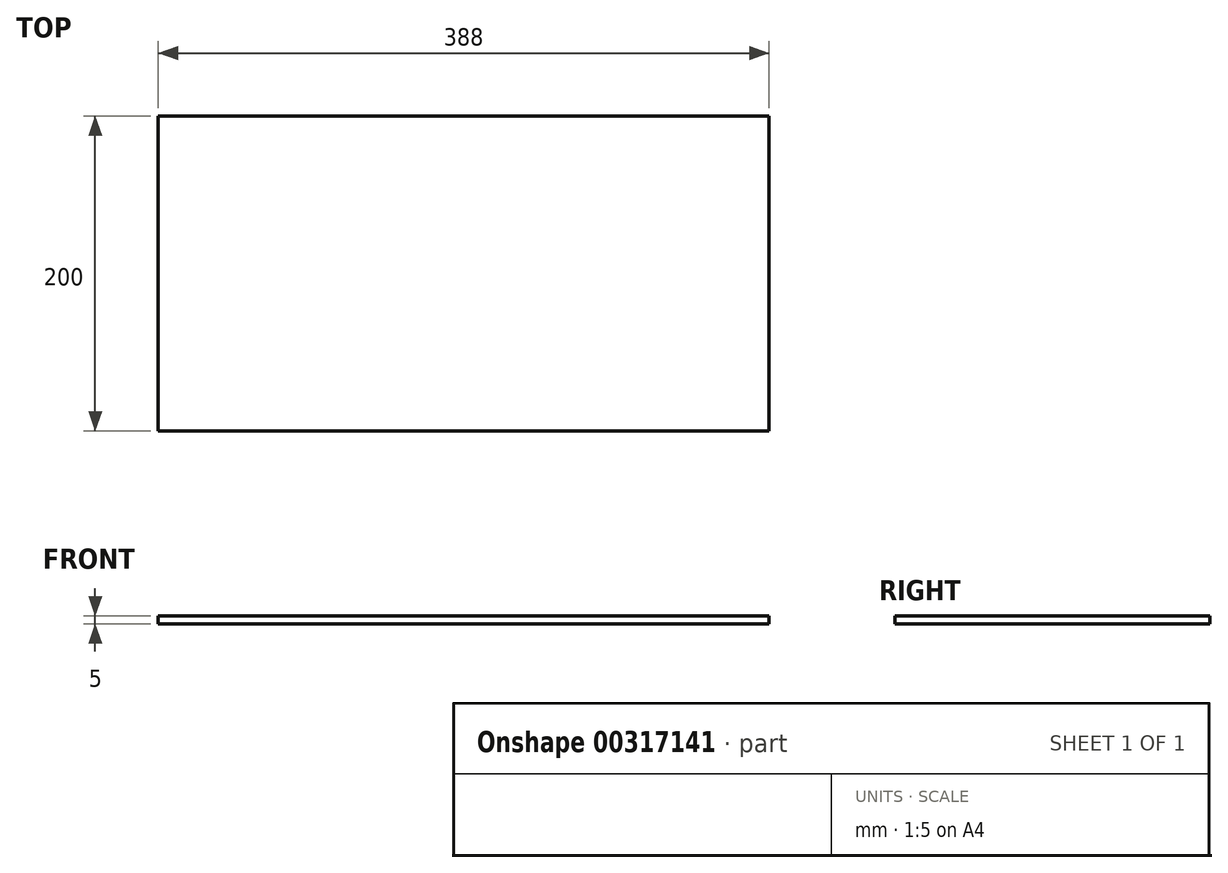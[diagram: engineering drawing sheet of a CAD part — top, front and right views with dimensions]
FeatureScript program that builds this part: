
annotation { "Feature Type Name" : "Feature", "Feature Type Description" : "" }
export const myFeature = defineFeature(function(context is Context, id is Id, definition is map)
    precondition{}
    {
        {
            var Q0;
            Q0=qCreatedBy(makeId("Top.planeOp"),FACE);
            var sketch = newSketch(context, id + "F0", { "sketchPlane" : qUnion([Q0])});
            skLineSegment(sketch, "E0.bottom", {"start": v(194, -100) * mm, "end": v(-194, -100) * mm});
            skLineSegment(sketch, "E0.top", {"start": v(194, 100) * mm, "end": v(-194, 100) * mm});
            skLineSegment(sketch, "E0.left", {"start": v(194, -100) * mm, "end": v(194, 100) * mm});
            skLineSegment(sketch, "E0.right", {"start": v(-194, -100) * mm, "end": v(-194, 100) * mm});
            skPoint(sketch, "E0.middle", {"position": v(0, 0) * mm});
            skSolve(sketch);
        }
        {
            var Q0;
            Q0=makeQuery(id+"F0.imprint","IMPRINT",FACE,{"disambiguationData":[TD([[makeQuery(id+"F0.imprint","IMPRINT",EDGE,{"derivedFrom":sQuery(id+"F0.wireOp",EDGE,"E0.bottom")}),-1.0]])]});
            extrude(context, id + "F1", {"entities" : qUnion([Q0]), "depth" : 5 * mm});
        }
    });
